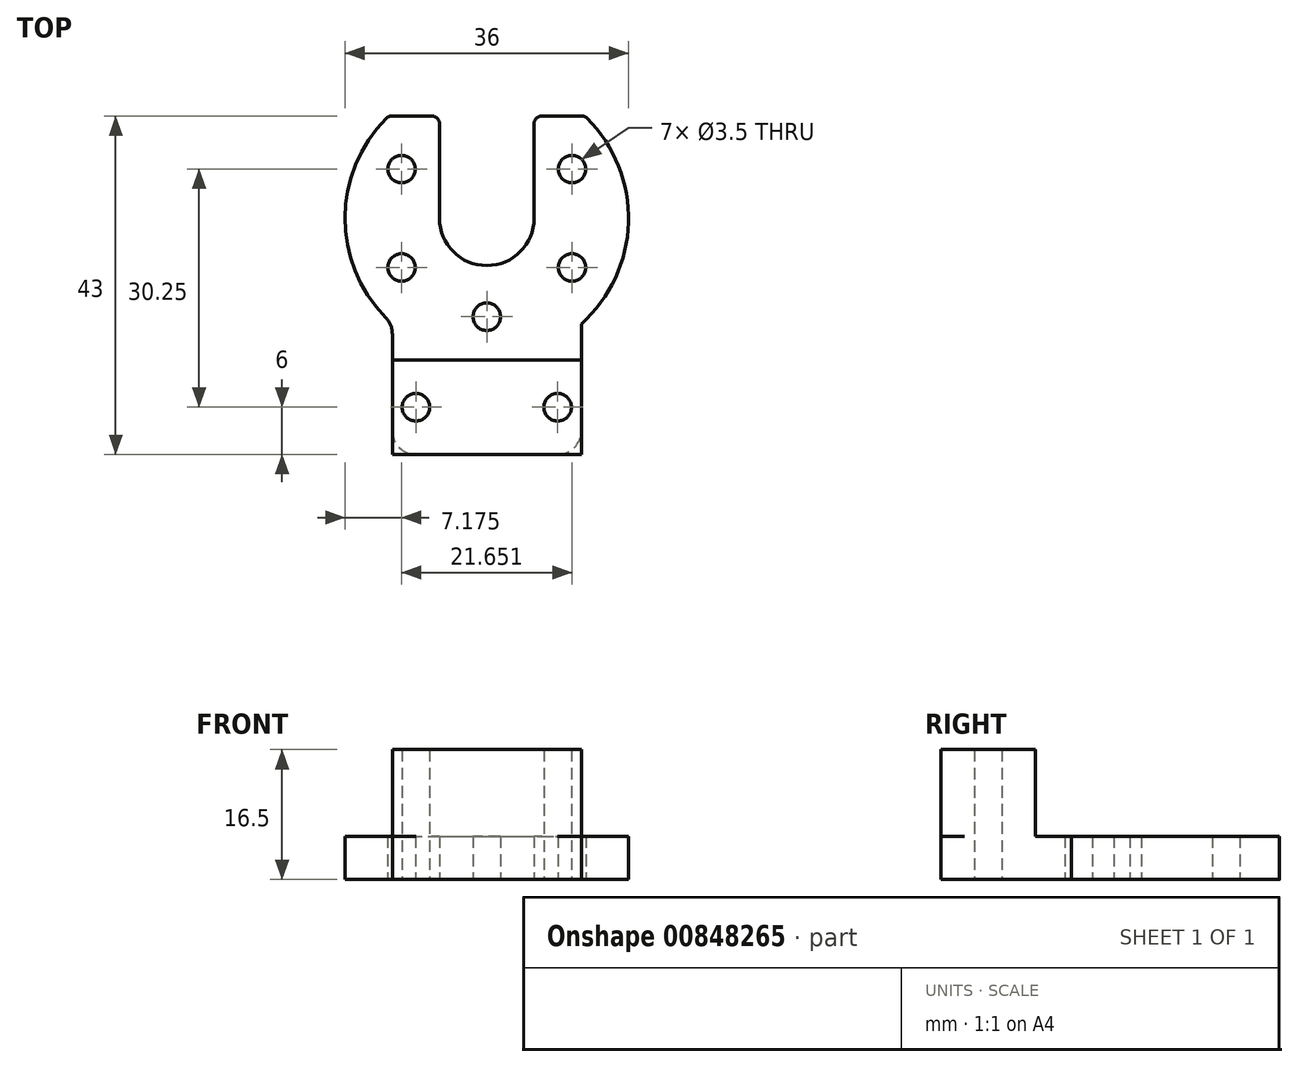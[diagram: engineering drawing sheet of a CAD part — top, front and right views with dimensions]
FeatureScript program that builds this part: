
annotation { "Feature Type Name" : "Feature", "Feature Type Description" : "" }
export const myFeature = defineFeature(function(context is Context, id is Id, definition is map)
    precondition{}
    {
        {
            var Q0;
            Q0=qCreatedBy(makeId("Top.planeOp"),FACE);
            var sketch = newSketch(context, id + "F0", { "sketchPlane" : qUnion([Q0])});
            skArc(sketch, "E0", {"start": v(-12.75, 12.7) * mm, "mid": v(0, -18) * mm, "end": v(12.75, 12.7) * mm});
            skArc(sketch, "E1", {"start": v(-6, 0) * mm, "mid": v(0, -6) * mm, "end": v(6, 0) * mm});
            skCircle(sketch, "E2", {"center": v(0, -12.5) * mm, "radius": 1.75 * mm});
            skCircle(sketch, "E3", {"center": v(10.83, 6.25) * mm, "radius": 1.75 * mm});
            skCircle(sketch, "E4", {"center": v(10.83, -6.25) * mm, "radius": 1.75 * mm});
            skCircle(sketch, "E5", {"center": v(-10.83, 6.25) * mm, "radius": 1.75 * mm});
            skCircle(sketch, "E6", {"center": v(-10.83, -6.25) * mm, "radius": 1.75 * mm});
            skLineSegment(sketch, "E7", {"start": v(-12.04, 13) * mm, "end": v(-7, 13) * mm});
            skLineSegment(sketch, "E8", {"start": v(6, 0) * mm, "end": v(6, 12) * mm});
            skLineSegment(sketch, "E9", {"start": v(-6, 0) * mm, "end": v(-6, 12) * mm});
            skLineSegment(sketch, "E10.trimOffspring", {"start": v(7, 13) * mm, "end": v(12.04, 13) * mm});
            skPoint(sketch, "E11.visualSharp", {"position": v(-6, 13) * mm});
            skArc(sketch, "E11.filletArc", {"start": v(-6, 12) * mm, "mid": v(-6.3, 12.7) * mm, "end": v(-7, 13) * mm});
            skPoint(sketch, "E12.visualSharp", {"position": v(6, 13) * mm});
            skArc(sketch, "E12.filletArc", {"start": v(7, 13) * mm, "mid": v(6.3, 12.7) * mm, "end": v(6, 12) * mm});
            skPoint(sketch, "E13.visualSharp", {"position": v(12.45, 13) * mm});
            skArc(sketch, "E13.filletArc", {"start": v(12.75, 12.7) * mm, "mid": v(12.43, 12.92) * mm, "end": v(12.04, 13) * mm});
            skPoint(sketch, "E14.visualSharp", {"position": v(-12.45, 13) * mm});
            skArc(sketch, "E14.filletArc", {"start": v(-12.04, 13) * mm, "mid": v(-12.43, 12.92) * mm, "end": v(-12.75, 12.7) * mm});
            skPoint(sketch, "E15.end.orphan", {"position": v(-8, 13) * mm});
            skPoint(sketch, "E16.start.orphan", {"position": v(-8, 0) * mm});
            skPoint(sketch, "E17.end.orphan", {"position": v(8, 13) * mm});
            skPoint(sketch, "E17.start.orphan", {"position": v(8, 0) * mm});
            skSolve(sketch);
        }
        {
            var Q0;
            Q0=qCreatedBy(makeId("Top.planeOp"),FACE);
            var sketch = newSketch(context, id + "F1", { "sketchPlane" : qUnion([Q0])});
            skArc(sketch, "E18.0", {"start": v(-12.75, 12.7) * mm, "mid": v(0, -18) * mm, "end": v(12.75, 12.7) * mm});
            skLineSegment(sketch, "E19.bottom", {"start": v(12, -30) * mm, "end": v(-12, -30) * mm});
            skLineSegment(sketch, "E19.left", {"start": v(12, -30) * mm, "end": v(12, -13.42) * mm});
            skLineSegment(sketch, "E19.right", {"start": v(-12, -30) * mm, "end": v(-12, -13.42) * mm});
            skPoint(sketch, "E19.middle", {"position": v(0, -18) * mm});
            skLineSegment(sketch, "E20", {"start": v(-12, -18) * mm, "end": v(12, -18) * mm});
            skPoint(sketch, "E21.orphan", {"position": v(12, -6) * mm});
            skPoint(sketch, "E22.orphan", {"position": v(-12, -6) * mm});
            skCircle(sketch, "E23", {"center": v(-9, -24) * mm, "radius": 1.75 * mm});
            skCircle(sketch, "E24", {"center": v(9, -24) * mm, "radius": 1.75 * mm});
            skSolve(sketch);
        }
        {
            var Q0;
            Q0=makeQuery(id+"F0.imprint","IMPRINT",FACE,{"disambiguationData":[TD([[makeQuery(id+"F0.imprint","IMPRINT",EDGE,{"derivedFrom":sQuery(id+"F0.wireOp",EDGE,"E0")}),1.0]])]});
            extrude(context, id + "F2", {"entities" : qUnion([Q0]), "depth" : 5.5 * mm, "offsetDistance" : 25 * mm});
        }
        {
            var Q0;
            {var subQ1=sQuery(id+"F1.wireOp",EDGE,"E19.bottom");Q0=makeQuery(id+"F1.imprint","IMPRINT",FACE,{"disambiguationData":[TD([[makeQuery(id+"F1.imprint","IMPRINT",EDGE,{"derivedFrom":subQ1}),-1.0]])]});}
            var Q1;
            {var subQ0=sQuery(id+"F1.wireOp",EDGE,"E19.left");var subQ1=sQuery(id+"F1.wireOp",EDGE,"E18.0");var subQ2=makeQuery(id+"F1.imprint","INTERSECT",VERTEX,{"derivedFrom":[subQ1,subQ0]});Q1=makeQuery(id+"F1.imprint","IMPRINT",FACE,{"disambiguationData":[TD([[makeQuery(id+"F1.imprint","IMPRINT",EDGE,{"disambiguationData":[TD([[subQ2,1.0]])],"derivedFrom":subQ1}),-1.0]])]});}
            var Q2;
            {var subQ0=sQuery(id+"F1.wireOp",EDGE,"E19.right");var subQ1=sQuery(id+"F1.wireOp",EDGE,"E18.0");var subQ2=makeQuery(id+"F1.imprint","INTERSECT",VERTEX,{"derivedFrom":[subQ1,subQ0]});Q2=makeQuery(id+"F1.imprint","IMPRINT",FACE,{"disambiguationData":[TD([[makeQuery(id+"F1.imprint","IMPRINT",EDGE,{"disambiguationData":[TD([[subQ2,-1.0]])],"derivedFrom":subQ1}),-1.0]])]});}
            extrude(context, id + "F3", {"entities" : qUnion([Q0, Q1, Q2]), "operationType" : NewBodyOperationType.ADD, "depth" : 5.5 * mm, "offsetDistance" : 25 * mm});
        }
        {
            var Q0;
            Q0=makeQuery(id+"F3.opExtrude","SWEPT_EDGE",EDGE,{"disambiguationData":[OSD([sQuery(id+"F1.wireOp",EDGE,"E18.0"),sQuery(id+"F1.wireOp",EDGE,"E19.right")])]});
            var Q1;
            Q1=makeQuery(id+"F3.opExtrude","SWEPT_EDGE",EDGE,{"disambiguationData":[OSD([sQuery(id+"F1.wireOp",EDGE,"E19.bottom"),sQuery(id+"F1.wireOp",EDGE,"E19.right")])]});
            var Q2;
            Q2=makeQuery(id+"F3.opExtrude","SWEPT_EDGE",EDGE,{"disambiguationData":[OSD([sQuery(id+"F1.wireOp",EDGE,"E18.0"),sQuery(id+"F1.wireOp",EDGE,"E19.left")])]});
            var Q3;
            Q3=makeQuery(id+"F3.opExtrude","SWEPT_EDGE",EDGE,{"disambiguationData":[OSD([sQuery(id+"F1.wireOp",EDGE,"E19.bottom"),sQuery(id+"F1.wireOp",EDGE,"E19.left")])]});
            fillet(context, id + "F4", {"entities" : qUnion([Q0, Q1, Q2, Q3]), "radius" : 3 * mm, "tangentPropagation" : true, "allowEdgeOverflow" : false});
        }
        {
            var Q0;
            Q0=makeQuery(id+"F3.boolean.opBoolean","MERGE",FACE,{"derivedFrom":[makeQuery(id+"F2.opExtrude","CAP_FACE",FACE,{"disambiguationData":[OSD([sQuery(id+"F0.wireOp",EDGE,"E0"),sQuery(id+"F0.wireOp",EDGE,"E1"),sQuery(id+"F0.wireOp",EDGE,"E2"),sQuery(id+"F0.wireOp",EDGE,"E3"),sQuery(id+"F0.wireOp",EDGE,"E4"),sQuery(id+"F0.wireOp",EDGE,"E5"),sQuery(id+"F0.wireOp",EDGE,"E6"),sQuery(id+"F0.wireOp",EDGE,"E7"),sQuery(id+"F0.wireOp",EDGE,"E8"),sQuery(id+"F0.wireOp",EDGE,"E9"),sQuery(id+"F0.wireOp",EDGE,"E10.trimOffspring"),sQuery(id+"F0.wireOp",EDGE,"E11.filletArc"),sQuery(id+"F0.wireOp",EDGE,"E12.filletArc"),sQuery(id+"F0.wireOp",EDGE,"E13.filletArc"),sQuery(id+"F0.wireOp",EDGE,"E14.filletArc")])],"isStart":false}),makeQuery(id+"F3.opExtrude","CAP_FACE",FACE,{"disambiguationData":[OSD([sQuery(id+"F1.wireOp",EDGE,"E18.0"),sQuery(id+"F1.wireOp",EDGE,"E19.bottom"),sQuery(id+"F1.wireOp",EDGE,"E19.left"),sQuery(id+"F1.wireOp",EDGE,"E19.right"),sQuery(id+"F1.wireOp",EDGE,"E23"),sQuery(id+"F1.wireOp",EDGE,"E24")])],"isStart":false})]});
            var sketch = newSketch(context, id + "F5", { "sketchPlane" : qUnion([Q0])});
            skLineSegment(sketch, "E25.0", {"start": v(-12, -18) * mm, "end": v(12, -18) * mm});
            skCircle(sketch, "E26.0", {"center": v(9, -24) * mm, "radius": 1.75 * mm});
            skCircle(sketch, "E26.1", {"center": v(-9, -24) * mm, "radius": 1.75 * mm});
            skLineSegment(sketch, "E26.2", {"start": v(-12, -30) * mm, "end": v(-12, -18) * mm});
            skLineSegment(sketch, "E26.3", {"start": v(12, -30) * mm, "end": v(-12, -30) * mm});
            skLineSegment(sketch, "E26.4", {"start": v(12, -30) * mm, "end": v(12, -18) * mm});
            skPoint(sketch, "E27.orphan", {"position": v(12, -13.42) * mm});
            skPoint(sketch, "E28.orphan", {"position": v(-12, -13.42) * mm});
            skSolve(sketch);
        }
        {
            var Q0;
            Q0=qSketchRegion(id+"F5",true);
            extrude(context, id + "F6", {"entities" : qUnion([Q0]), "operationType" : NewBodyOperationType.ADD, "depth" : 11 * mm, "offsetDistance" : 25 * mm});
        }
    });
